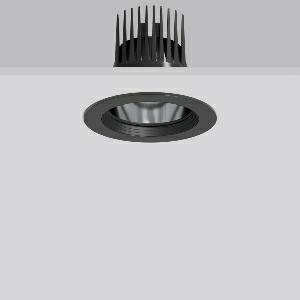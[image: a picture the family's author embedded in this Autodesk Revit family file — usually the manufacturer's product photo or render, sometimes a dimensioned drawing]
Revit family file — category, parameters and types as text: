
# Revit family: heledon_maxi_e_901766_003_1_76_e380
name_source: partatom
category: Lighting Fixtures
units: mm (PartAtom-declared; Revit-internal decimal feet)

## family parameters
Cut with Voids When Loaded = No
Host = Face
Light Source = No
Part Type = Normal
Room Calculation Point = No
Round Connector Dimension = Use Diameter
Shared = No

## types (1)
- HELEDON maxi E (1 x LED Modul 940, 4400 lm, 4000)
    Apparent Load = 35 VA
    Approval mark = CE
    CIE Flux Codes = 97 100 100 100 100
    Color Rendering = 92
    Color Temperature = 4000
    Default Elevation = 1800 mm
    Description = Series: HELEDON maxi
Round recessed downlight. Housing: die-cast aluminium, powder-coated. Black plastic ring and recessed LED to prevent glare from the side. Optical assembly with reflector made of MIRO-Silver with 98% total light reflection for outstanding efficiency - can be changed without tools. Best colour rendering index Ra>90. Suitable for Recessed ceiling mounting. Installation without tools thanks to spring fastening system. Including separate LED converter with connecting cable 600 mm.High quality converter without flickering and stroboscopic effect. Through-wiring box (5 pole) available as accessory. The following accessories can be mounted without use of tools: interchangeable lenses, decorative glasses, honeycomb louvre, clear and frosted diffusers, white interchangeable plastic ring. 
Colour: deep black, matt (RAL 9005)
Diameter: 162 mm
Height: 3 mm
Cut-out diameter: 152 mm
Recess height: 200 mm
Luminaire: recess height: 135 mm
Lamp: LED
Socket: without socket
Colour temperature: 4000K
Colour rendering index (CRI): 92
System power: 35 W
Rated luminous flux: 4400 lm
Luminous efficiency: 126 lm/W
Control gear: Converter, dimmable, DALI
Protection class: II
Type of protection: IP 20
    Height = 0 mm  [stored 0 ft]
    Lamp = 1 x LED Modul 940
    Lamp Light Flux = 4400 lm
    Lamp count = 1
    Length = 162 mm
    Lifetime = 50000 h
    Luminous efficacy = 126 lm/W
    Manufacturer = RZB
    ModVariant = No
    Model = 901766.003.1.76
    Mounting Place = Ceiling
    Mounting Type = Recessed
    Number of Poles = 1
    OnlyDefault = Yes
    Power Factor = 1
    Product Name = HELEDON maxi E
    Product group = Recessed downlights
    ProductGroupID = 402
    Protection Class = Protection class II
    Protection Degree = IP 20
    RLX_Detail_Level = 1
    RLX_Emergency_Light_Flux = 0 lm
    RLX_Emergency_Type = 0
    RLX_Emergency_Type_DB = No
    RlxData = <blob elided: 123277 chars, md5=5cf9feaa>
    Socket = socket
    Standby Power = 0 W
    System Light Flux = 4400 lm
    System Power = 35 W
    Type Comments = Product without accessories
    Type Image = 901662.003.jpg
    URL = http://relux.com
    VarID = ---
    Voltage = 230 V
    Voltage Range = 220-240 V
    Weight = 0.00 kg
    Width = 0 mm  [stored 0 ft]

note: [stored X ft] marks values corroborated as IEEE doubles in the binary element streams (Revit-internal decimal feet)

## geometry (parser evidence)
native form markers: Blend x4, Sweep x10
no freeform markers — native parametric forms only
